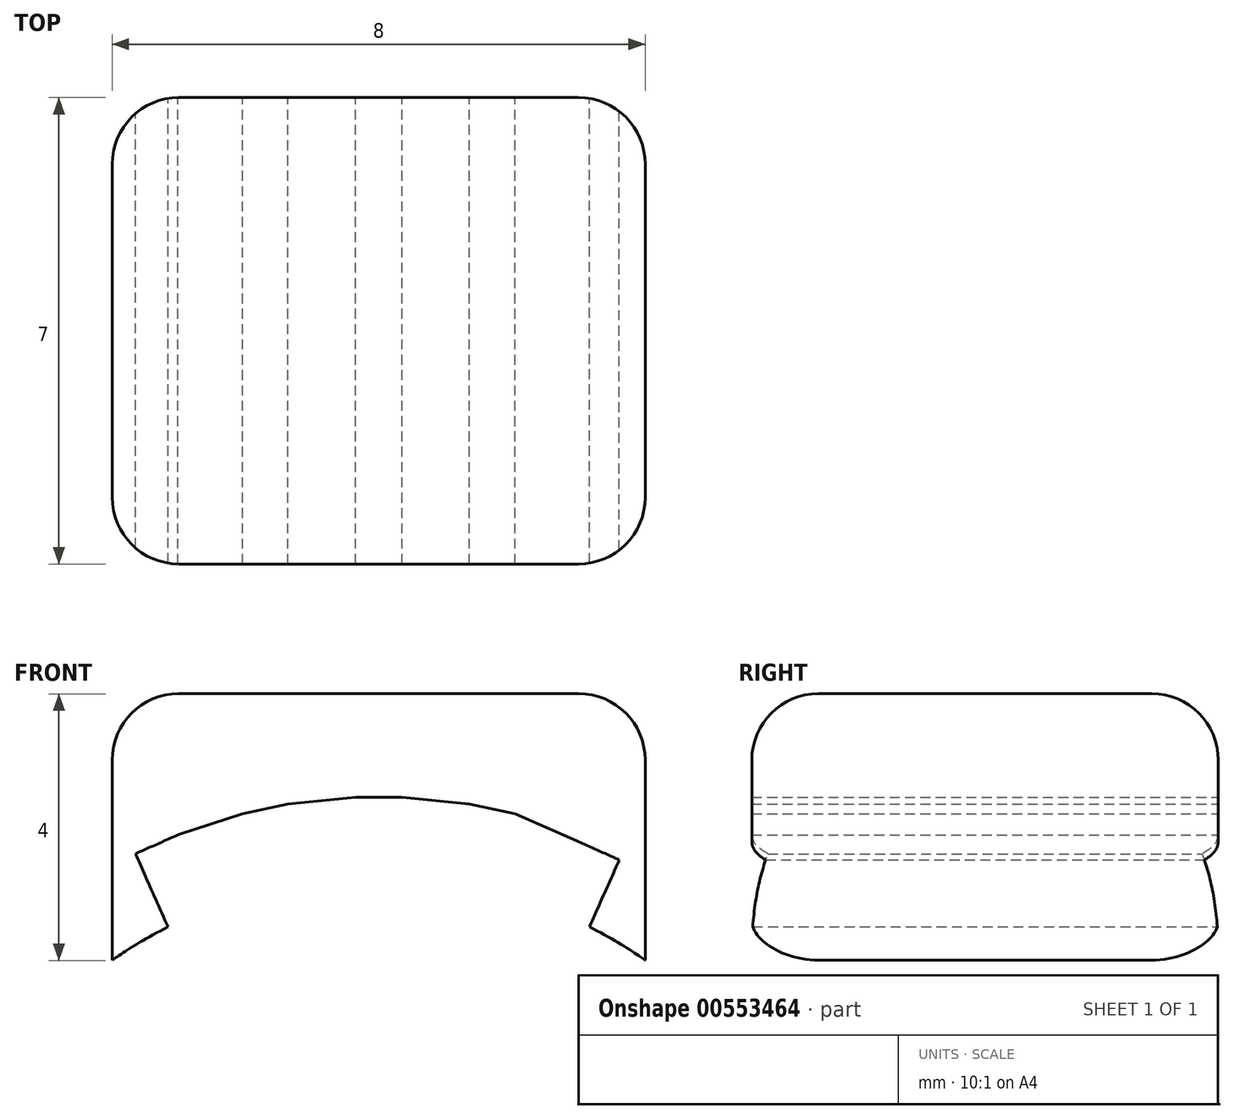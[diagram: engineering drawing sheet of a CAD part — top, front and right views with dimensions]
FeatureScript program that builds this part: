
annotation { "Feature Type Name" : "Feature", "Feature Type Description" : "" }
export const myFeature = defineFeature(function(context is Context, id is Id, definition is map)
    precondition{}
    {
        {
            var Q0;
            Q0=qCreatedBy(makeId("Front.planeOp"),FACE);
            var sketch = newSketch(context, id + "F0", { "sketchPlane" : qUnion([Q0])});
            skArc(sketch, "E0", {"start": v(4, 5.74) * mm, "mid": v(3.6, 6) * mm, "end": v(3.16, 6.24) * mm});
            skLineSegment(sketch, "E1.bottom", {"start": v(-4, 9.74) * mm, "end": v(4, 9.74) * mm});
            skLineSegment(sketch, "E1.left", {"start": v(-4, 9.74) * mm, "end": v(-4, 5.74) * mm});
            skLineSegment(sketch, "E1.right", {"start": v(4, 9.74) * mm, "end": v(4, 5.74) * mm});
            skLineSegment(sketch, "E2.top", {"start": v(-0.35, 8.2) * mm, "end": v(0.35, 8.2) * mm});
            skLineSegment(sketch, "E2.left", {"start": v(-0.35, 7) * mm, "end": v(-0.35, 8.2) * mm, "construction": true});
            skLineSegment(sketch, "E2.right", {"start": v(0.35, 7) * mm, "end": v(0.35, 8.2) * mm, "construction": true});
            skArc(sketch, "E3.trimOffspring", {"start": v(-0.35, 7) * mm, "mid": v(-0.73, 6.96) * mm, "end": v(-1.11, 6.91) * mm, "construction": true});
            skLineSegment(sketch, "E4", {"start": v(0, 0) * mm, "end": v(-2.93, 13.8) * mm, "construction": true});
            skLineSegment(sketch, "E5", {"start": v(0, 0) * mm, "end": v(2.92, 13.72) * mm, "construction": true});
            skLineSegment(sketch, "E6", {"start": v(-1.8, 6.77) * mm, "end": v(-2.05, 7.94) * mm, "construction": true});
            skLineSegment(sketch, "E7", {"start": v(-2.05, 7.94) * mm, "end": v(-1.36, 8.09) * mm});
            skLineSegment(sketch, "E8", {"start": v(-1.36, 8.09) * mm, "end": v(-1.11, 6.91) * mm, "construction": true});
            skArc(sketch, "E9.trimOffspring", {"start": v(-1.8, 6.77) * mm, "mid": v(-2.16, 6.66) * mm, "end": v(-2.52, 6.53) * mm, "construction": true});
            skLineSegment(sketch, "E10", {"start": v(1.11, 6.91) * mm, "end": v(1.36, 8.09) * mm, "construction": true});
            skLineSegment(sketch, "E11", {"start": v(1.36, 8.09) * mm, "end": v(2.05, 7.94) * mm});
            skLineSegment(sketch, "E12", {"start": v(2.05, 7.94) * mm, "end": v(1.8, 6.77) * mm, "construction": true});
            skArc(sketch, "E13.trimOffspring", {"start": v(1.11, 6.91) * mm, "mid": v(0.73, 6.96) * mm, "end": v(0.35, 7) * mm, "construction": true});
            skLineSegment(sketch, "E14", {"start": v(0, 0) * mm, "end": v(5.8, 13) * mm, "construction": true});
            skLineSegment(sketch, "E15", {"start": v(0, 0) * mm, "end": v(-5.84, 13.12) * mm, "construction": true});
            skLineSegment(sketch, "E16", {"start": v(-3.16, 6.24) * mm, "end": v(-3.65, 7.34) * mm});
            skLineSegment(sketch, "E17", {"start": v(-3.65, 7.34) * mm, "end": v(-3.01, 7.63) * mm});
            skLineSegment(sketch, "E18", {"start": v(-3.01, 7.63) * mm, "end": v(-2.52, 6.53) * mm, "construction": true});
            skArc(sketch, "E19.trimOffspring", {"start": v(-3.16, 6.24) * mm, "mid": v(-3.6, 6) * mm, "end": v(-4, 5.74) * mm});
            skLineSegment(sketch, "E20", {"start": v(2.52, 6.53) * mm, "end": v(2.97, 7.53) * mm, "construction": true});
            skLineSegment(sketch, "E21", {"start": v(2.97, 7.53) * mm, "end": v(3.61, 7.25) * mm});
            skLineSegment(sketch, "E22", {"start": v(3.61, 7.25) * mm, "end": v(3.16, 6.24) * mm});
            skArc(sketch, "E23.trimOffspring", {"start": v(2.52, 6.53) * mm, "mid": v(2.16, 6.66) * mm, "end": v(1.8, 6.77) * mm, "construction": true});
            skLineSegment(sketch, "E24", {"start": v(-3.01, 7.63) * mm, "end": v(-2.05, 7.94) * mm});
            skLineSegment(sketch, "E25", {"start": v(-1.36, 8.09) * mm, "end": v(-0.35, 8.2) * mm});
            skLineSegment(sketch, "E26", {"start": v(0.35, 8.2) * mm, "end": v(1.36, 8.09) * mm});
            skLineSegment(sketch, "E27", {"start": v(2.05, 7.94) * mm, "end": v(2.97, 7.53) * mm});
            skSolve(sketch);
        }
        {
            var Q0;
            Q0 = qSketchRegion(id + "F0", true);
            extrude(context, id + "F1", {"entities" : qUnion([Q0]), "depth" : 7 * mm, "offsetDistance" : 25 * mm});
        }
        {
            var Q0;
            Q0=makeQuery(id+"F1.opExtrude","CAP_EDGE",EDGE,{"disambiguationData":[OSD([sQuery(id+"F0.wireOp",EDGE,"E1.left")])],"isStart":false});
            var Q1;
            Q1=makeQuery(id+"F1.opExtrude","CAP_EDGE",EDGE,{"disambiguationData":[OSD([sQuery(id+"F0.wireOp",EDGE,"E1.right")])],"isStart":false});
            var Q2;
            Q2=makeQuery(id+"F1.opExtrude","CAP_EDGE",EDGE,{"disambiguationData":[OSD([sQuery(id+"F0.wireOp",EDGE,"E1.right")])],"isStart":true});
            var Q3;
            Q3=makeQuery(id+"F1.opExtrude","CAP_EDGE",EDGE,{"disambiguationData":[OSD([sQuery(id+"F0.wireOp",EDGE,"E1.left")])],"isStart":true});
            var Q4;
            Q4=makeQuery(id+"F1.opExtrude","SWEPT_FACE",FACE,{"disambiguationData":[OSD([sQuery(id+"F0.wireOp",EDGE,"E1.bottom")])]});
            fillet(context, id + "F2", {"entities" : qUnion([Q0, Q1, Q2, Q3, Q4]), "radius" : 1 * mm, "tangentPropagation" : true, "allowEdgeOverflow" : false});
        }
    });
